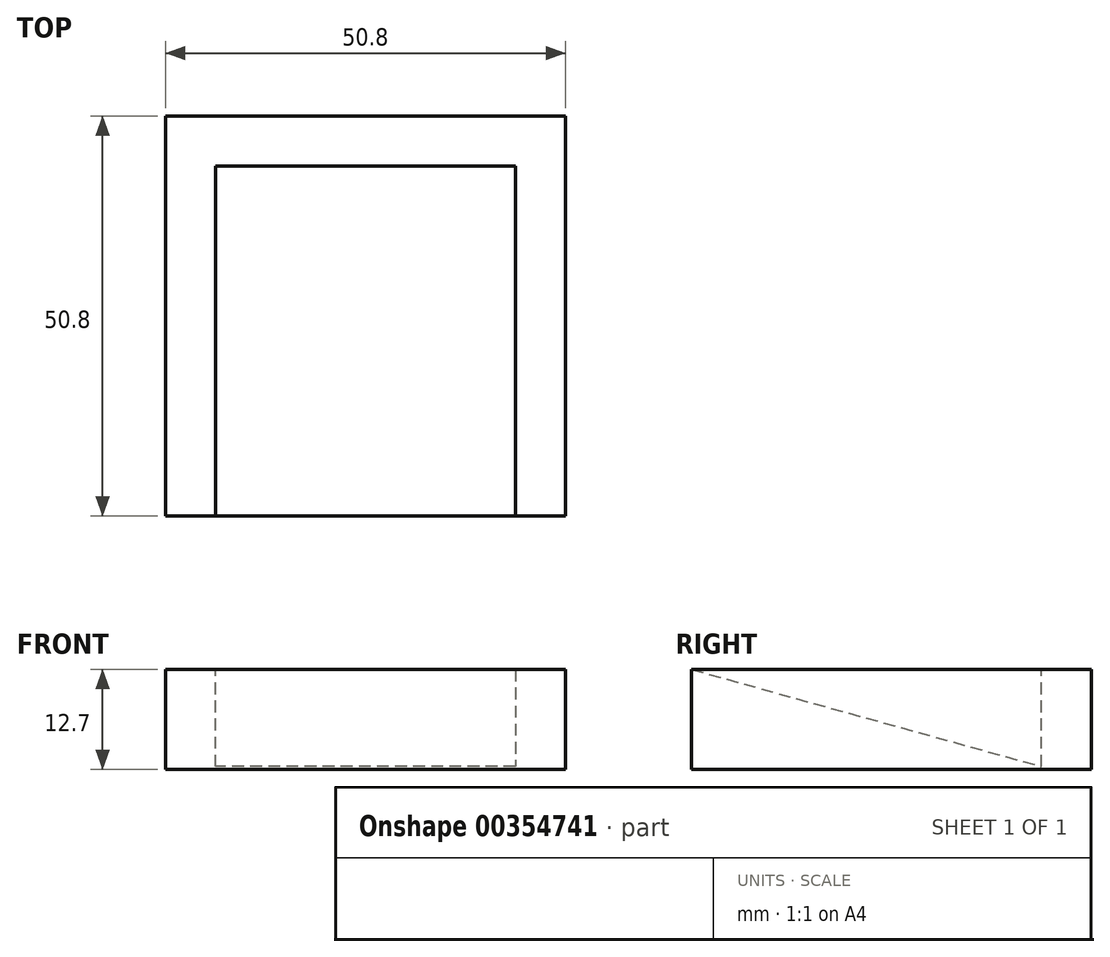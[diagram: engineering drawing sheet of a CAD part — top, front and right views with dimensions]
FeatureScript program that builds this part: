
annotation { "Feature Type Name" : "Feature", "Feature Type Description" : "" }
export const myFeature = defineFeature(function(context is Context, id is Id, definition is map)
    precondition{}
    {
        {
            var Q0;
            Q0=qCreatedBy(makeId("Top.planeOp"),FACE);
            var sketch = newSketch(context, id + "F0", { "sketchPlane" : qUnion([Q0])});
            skLineSegment(sketch, "E0.bottom", {"start": v(25.4, -25.4) * mm, "end": v(-25.4, -25.4) * mm});
            skLineSegment(sketch, "E0.top", {"start": v(25.4, 25.4) * mm, "end": v(-25.4, 25.4) * mm});
            skLineSegment(sketch, "E0.left", {"start": v(25.4, -25.4) * mm, "end": v(25.4, 25.4) * mm});
            skLineSegment(sketch, "E0.right", {"start": v(-25.4, -25.4) * mm, "end": v(-25.4, 25.4) * mm});
            skPoint(sketch, "E0.middle", {"position": v(0, 0) * mm});
            skSolve(sketch);
        }
        {
            var Q0;
            Q0=makeQuery(id+"F0.imprint","IMPRINT",FACE,{"disambiguationData":[TD([[makeQuery(id+"F0.imprint","IMPRINT",EDGE,{"derivedFrom":sQuery(id+"F0.wireOp",EDGE,"E0.bottom")}),-1.0]])]});
            extrude(context, id + "F1", {"entities" : qUnion([Q0]), "depth" : 12.7 * mm});
        }
        {
            var Q0;
            Q0=makeQuery(id+"F1.opExtrude","CAP_FACE",FACE,{"disambiguationData":[OSD([sQuery(id+"F0.wireOp",EDGE,"E0.bottom"),sQuery(id+"F0.wireOp",EDGE,"E0.top"),sQuery(id+"F0.wireOp",EDGE,"E0.left"),sQuery(id+"F0.wireOp",EDGE,"E0.right")])],"isStart":false});
            var sketch = newSketch(context, id + "F2", { "sketchPlane" : qUnion([Q0])});
            skLineSegment(sketch, "E1.bottom", {"start": v(19.05, -69.85) * mm, "end": v(-19.05, -69.85) * mm});
            skLineSegment(sketch, "E1.top", {"start": v(19.05, 19.05) * mm, "end": v(-19.05, 19.05) * mm});
            skLineSegment(sketch, "E1.left", {"start": v(19.05, -69.85) * mm, "end": v(19.05, 19.05) * mm});
            skLineSegment(sketch, "E1.right", {"start": v(-19.05, -69.85) * mm, "end": v(-19.05, 19.05) * mm});
            skPoint(sketch, "E1.middle", {"position": v(0, -25.4) * mm});
            skSolve(sketch);
        }
        {
            var Q0;
            {var subQ0=sQuery(id+"F2.wireOp",EDGE,"E1.top");Q0=makeQuery(id+"F2.imprint","IMPRINT",FACE,{"disambiguationData":[TD([[makeQuery(id+"F2.imprint","IMPRINT",EDGE,{"derivedFrom":subQ0}),1.0]])]});}
            extrude(context, id + "F3", {"entities" : qUnion([Q0]), "operationType" : NewBodyOperationType.REMOVE, "oppositeDirection" : true, "depth" : 25.4 * mm});
        }
        {
            var Q0;
            Q0=makeQuery(id+"F1.opExtrude","SWEPT_FACE",FACE,{"disambiguationData":[OSD([sQuery(id+"F0.wireOp",EDGE,"E0.left")])]});
            var sketch = newSketch(context, id + "F4", { "sketchPlane" : qUnion([Q0])});
            skLineSegment(sketch, "E2", {"start": v(-25.4, 12.7) * mm, "end": v(20.34, 0) * mm});
            skLineSegment(sketch, "E3", {"start": v(20.34, 0) * mm, "end": v(-25.4, 0) * mm});
            skLineSegment(sketch, "E4", {"start": v(-25.4, 0) * mm, "end": v(-25.4, 12.7) * mm});
            skSolve(sketch);
        }
        {
            var Q0;
            Q0=makeQuery(id+"F4.imprint","IMPRINT",FACE,{"disambiguationData":[TD([[makeQuery(id+"F4.imprint","IMPRINT",EDGE,{"derivedFrom":sQuery(id+"F4.wireOp",EDGE,"E2")}),-1.0]])]});
            extrude(context, id + "F5", {"entities" : qUnion([Q0]), "operationType" : NewBodyOperationType.ADD, "oppositeDirection" : true, "depth" : 47.75 * mm});
        }
    });
